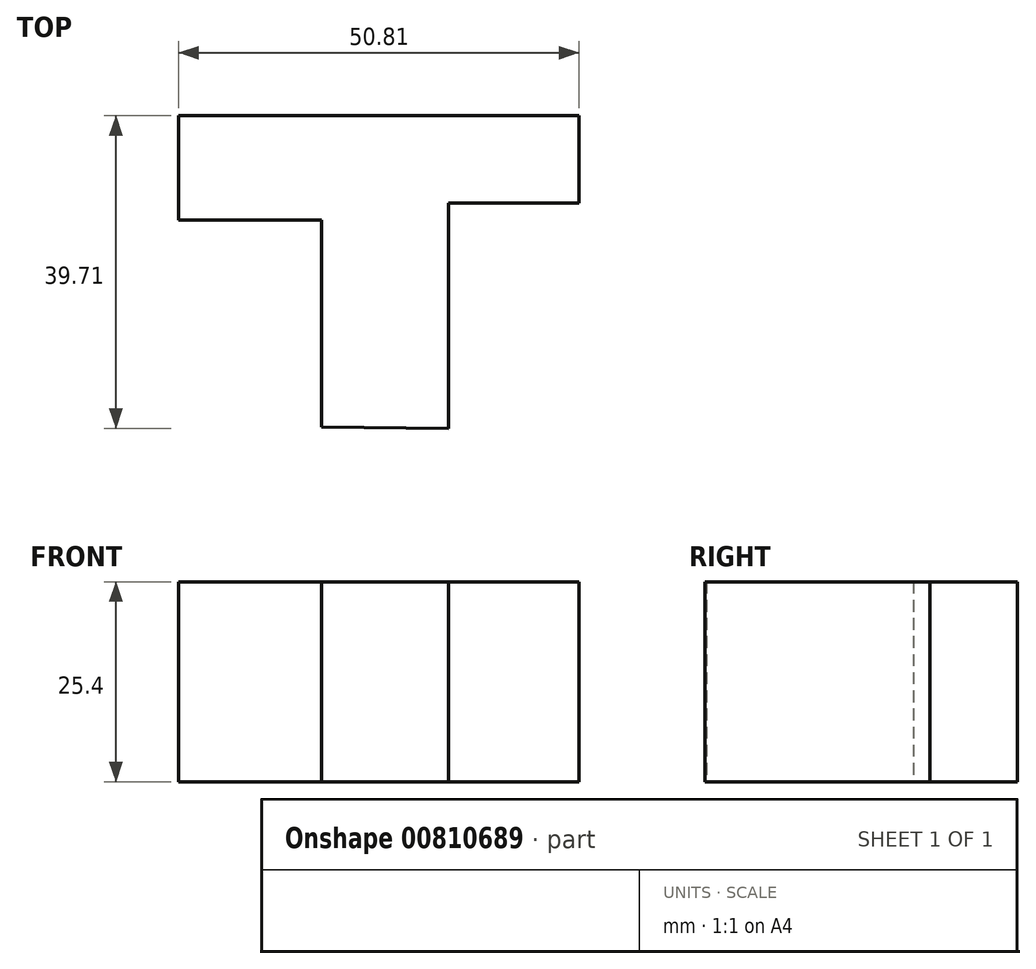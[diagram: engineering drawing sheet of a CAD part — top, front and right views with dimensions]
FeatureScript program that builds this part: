
annotation { "Feature Type Name" : "Feature", "Feature Type Description" : "" }
export const myFeature = defineFeature(function(context is Context, id is Id, definition is map)
    precondition{}
    {
        {
            var Q0;
            Q0=qCreatedBy(makeId("Top.planeOp"),FACE);
            var sketch = newSketch(context, id + "F0", { "sketchPlane" : qUnion([Q0])});
            skLineSegment(sketch, "E0", {"start": v(0, 23.26) * mm, "end": v(-26.38, 23.26) * mm});
            skLineSegment(sketch, "E1", {"start": v(-26.38, 23.26) * mm, "end": v(-26.38, 10.03) * mm});
            skLineSegment(sketch, "E2", {"start": v(-26.38, 10.03) * mm, "end": v(-8.27, 10.03) * mm});
            skLineSegment(sketch, "E3", {"start": v(0, 23.26) * mm, "end": v(24.43, 23.26) * mm});
            skLineSegment(sketch, "E4", {"start": v(24.43, 23.26) * mm, "end": v(24.43, 12.17) * mm});
            skLineSegment(sketch, "E5", {"start": v(24.43, 12.17) * mm, "end": v(7.88, 12.17) * mm});
            skLineSegment(sketch, "E6", {"start": v(7.88, 12.17) * mm, "end": v(7.88, -16.45) * mm});
            skLineSegment(sketch, "E7", {"start": v(-8.27, 10.03) * mm, "end": v(-8.27, -16.26) * mm});
            skLineSegment(sketch, "E8", {"start": v(-8.27, -16.26) * mm, "end": v(7.88, -16.45) * mm});
            skSolve(sketch);
        }
        {
            var Q0;
            Q0=makeQuery(id+"F0.imprint","IMPRINT",FACE,{"disambiguationData":[TD([[makeQuery(id+"F0.imprint","IMPRINT",EDGE,{"derivedFrom":sQuery(id+"F0.wireOp",EDGE,"E0")}),1.0]])]});
            extrude(context, id + "F1", {"entities" : qUnion([Q0]), "depth" : 25.4 * mm, "offsetDistance" : 25.4 * mm});
        }
    });
